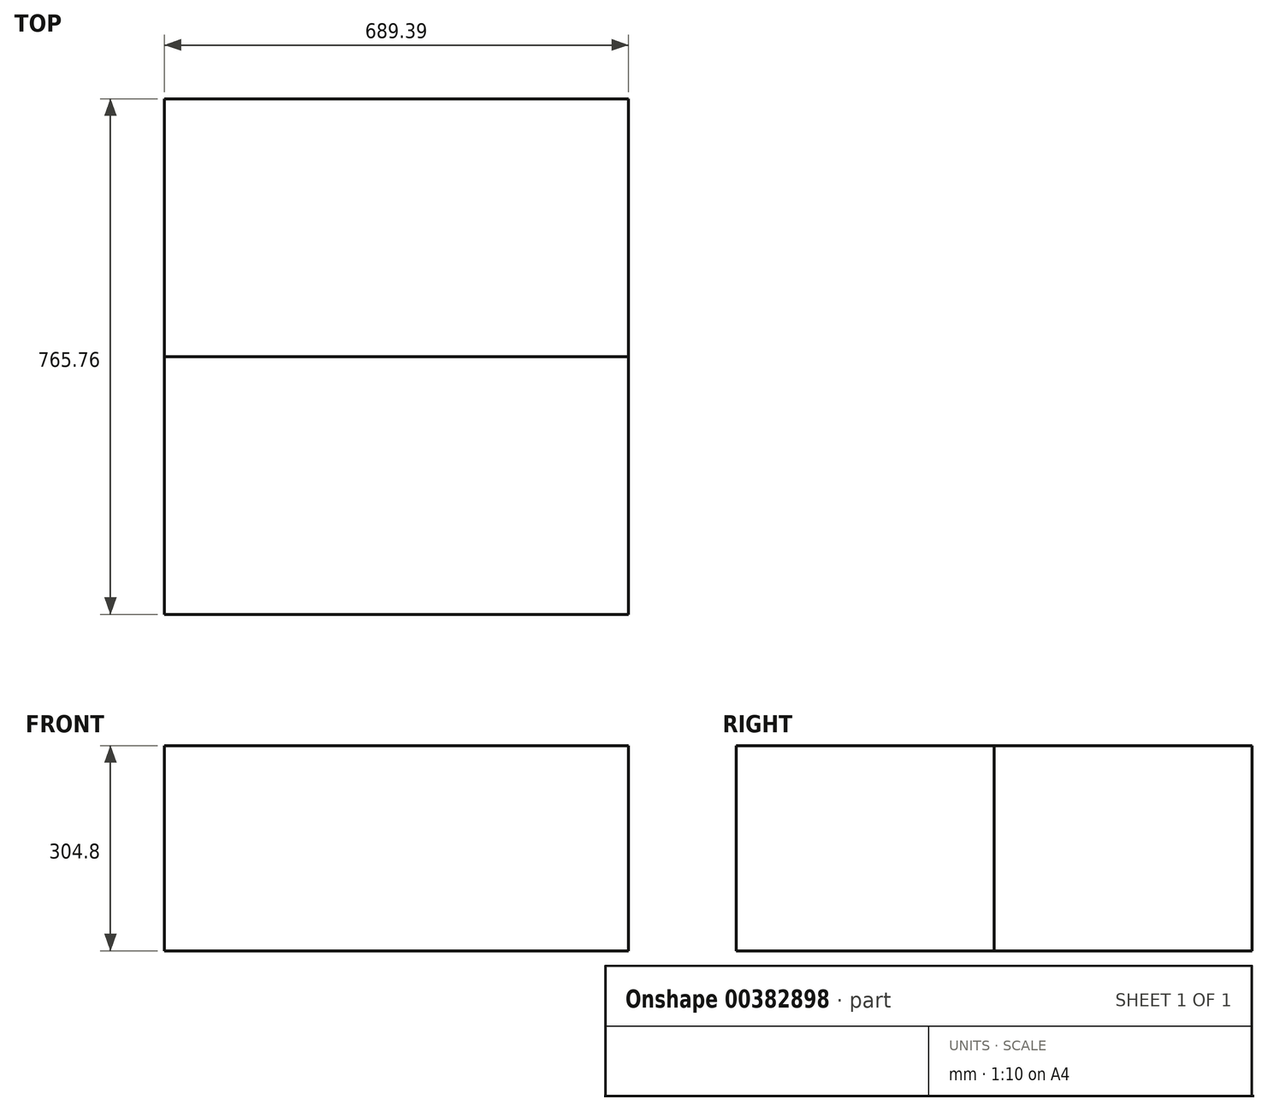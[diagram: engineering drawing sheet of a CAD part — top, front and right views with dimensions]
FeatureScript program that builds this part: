
annotation { "Feature Type Name" : "Feature", "Feature Type Description" : "" }
export const myFeature = defineFeature(function(context is Context, id is Id, definition is map)
    precondition{}
    {
        {
            var Q0;
            Q0=qCreatedBy(makeId("Top.planeOp"),FACE);
            var sketch = newSketch(context, id + "F0", { "sketchPlane" : qUnion([Q0])});
            skLineSegment(sketch, "E0.bottom", {"start": v(276.07, 141.77) * mm, "end": v(-413.32, 141.77) * mm});
            skLineSegment(sketch, "E0.top", {"start": v(276.07, -241.1) * mm, "end": v(-413.32, -241.1) * mm});
            skLineSegment(sketch, "E0.left", {"start": v(276.07, 141.77) * mm, "end": v(276.07, -241.1) * mm});
            skLineSegment(sketch, "E0.right", {"start": v(-413.32, 141.77) * mm, "end": v(-413.32, -241.1) * mm});
            skSolve(sketch);
        }
        {
            var Q0;
            Q0=makeQuery(id+"F0.imprint","IMPRINT",FACE,{"disambiguationData":[TD([[makeQuery(id+"F0.imprint","IMPRINT",EDGE,{"derivedFrom":sQuery(id+"F0.wireOp",EDGE,"E0.bottom")}),1.0]])]});
            extrude(context, id + "F1", {"entities" : qUnion([Q0]), "depth" : 304.8 * mm});
        }
        {
            var Q0;
            Q0=makeQuery(id+"F1.opExtrude","SWEPT_BODY",BODY,{"disambiguationData":[OSD([sQuery(id+"F0.wireOp",EDGE,"E0.bottom"),sQuery(id+"F0.wireOp",EDGE,"E0.top"),sQuery(id+"F0.wireOp",EDGE,"E0.left"),sQuery(id+"F0.wireOp",EDGE,"E0.right")])]});
            var Q1;
            Q1=makeQuery(id+"F1.opExtrude","SWEPT_FACE",FACE,{"disambiguationData":[OSD([sQuery(id+"F0.wireOp",EDGE,"E0.top")])]});
            mirror(context, id + "F2", {"entities" : qUnion([Q0]), "mirrorPlane" : qUnion([Q1])});
        }
    });
